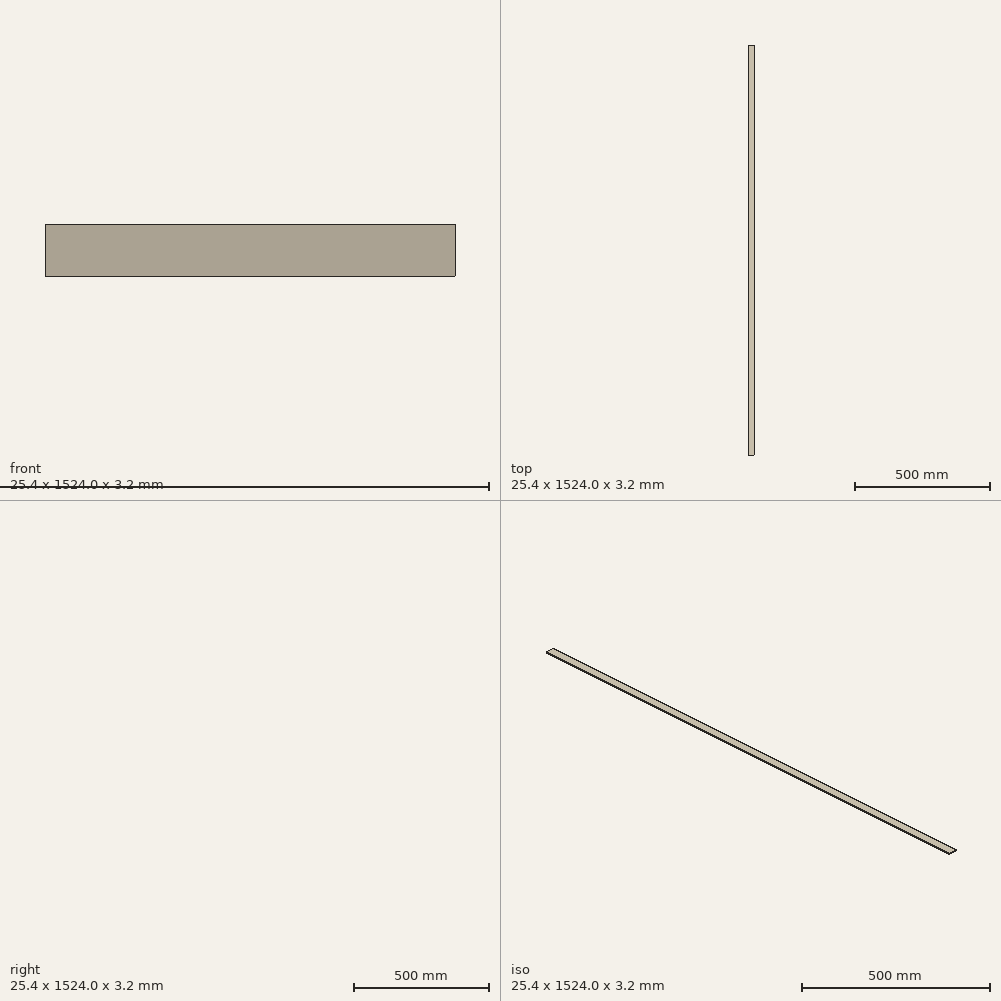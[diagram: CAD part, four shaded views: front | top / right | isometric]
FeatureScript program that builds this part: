
annotation { "Feature Type Name" : "Feature", "Feature Type Description" : "" }
export const myFeature = defineFeature(function(context is Context, id is Id, definition is map)
    precondition{}
    {
        {
            var Q0;
            Q0=qCreatedBy(makeId("Top.planeOp"),FACE);
            var sketch = newSketch(context, id + "F0", { "sketchPlane" : qUnion([Q0])});
            skLineSegment(sketch, "E0.bottom", {"start": v(12.7, 762) * mm, "end": v(-12.7, 762) * mm});
            skLineSegment(sketch, "E0.top", {"start": v(12.7, -762) * mm, "end": v(-12.7, -762) * mm});
            skLineSegment(sketch, "E0.left", {"start": v(12.7, 762) * mm, "end": v(12.7, -762) * mm});
            skLineSegment(sketch, "E0.right", {"start": v(-12.7, 762) * mm, "end": v(-12.7, -762) * mm});
            skPoint(sketch, "E0.middle", {"position": v(0, 0) * mm});
            skSolve(sketch);
        }
        {
            var Q0;
            Q0=makeQuery(id+"F0.imprint","IMPRINT",FACE,{"disambiguationData":[TD([[makeQuery(id+"F0.imprint","IMPRINT",EDGE,{"derivedFrom":sQuery(id+"F0.wireOp",EDGE,"E0.bottom")}),1.0]])]});
            extrude(context, id + "F1", {"entities" : qUnion([Q0]), "depth" : 3.17 * mm, "offsetDistance" : 25.4 * mm});
        }
    });
